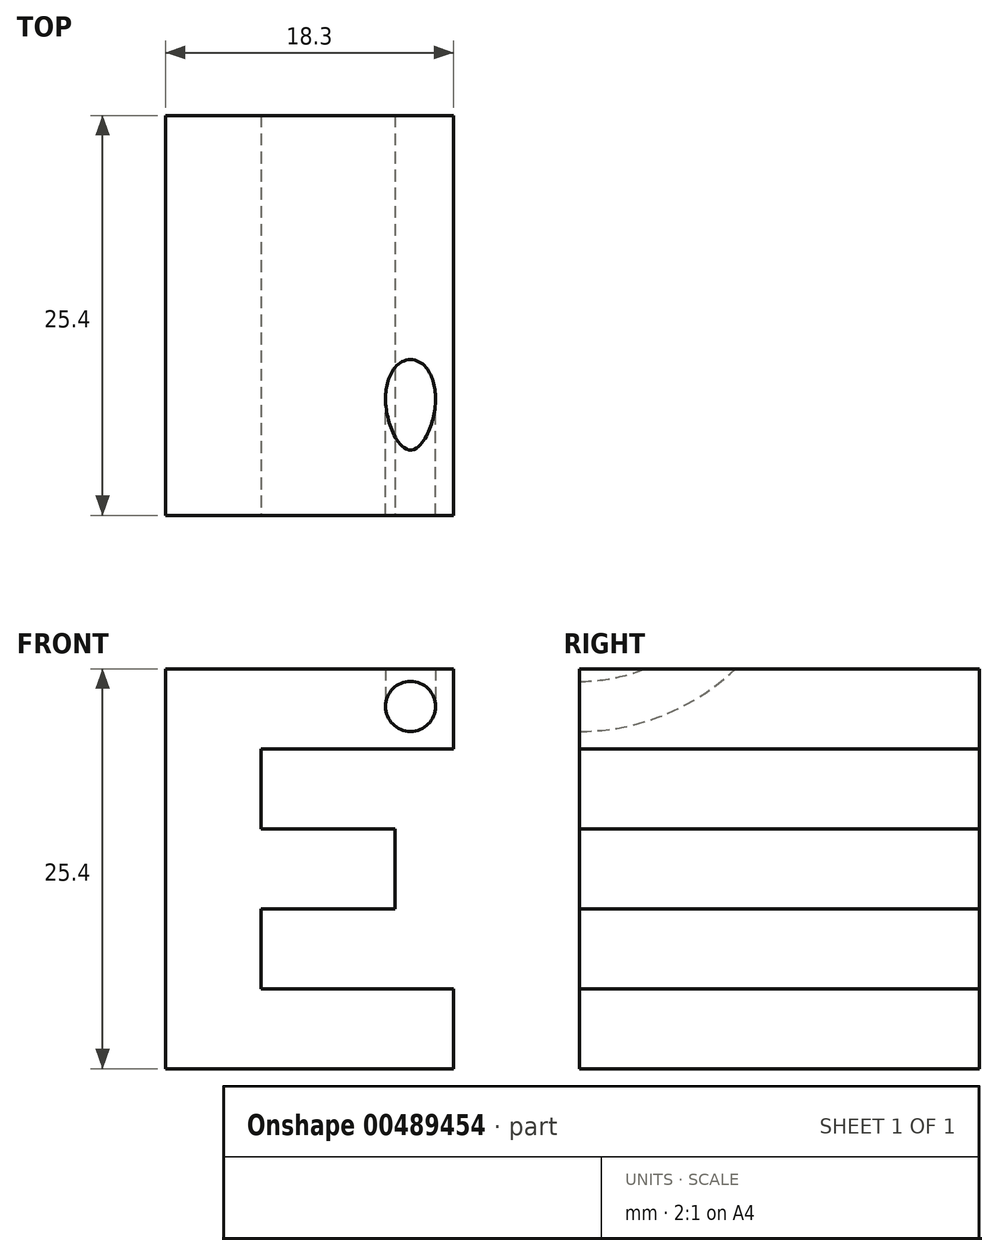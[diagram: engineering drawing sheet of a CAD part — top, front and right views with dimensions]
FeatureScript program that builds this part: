
annotation { "Feature Type Name" : "Feature", "Feature Type Description" : "" }
export const myFeature = defineFeature(function(context is Context, id is Id, definition is map)
    precondition{}
    {
        {
            var Q0;
            Q0=qCreatedBy(makeId("Front.planeOp"),FACE);
            var sketch = newSketch(context, id + "F0", { "sketchPlane" : qUnion([Q0])});
            skLineSegment(sketch, "E0", {"start": v(0, 0) * mm, "end": v(25.4, 0) * mm});
            skLineSegment(sketch, "E1", {"start": v(25.4, 0) * mm, "end": v(25.4, 25.4) * mm});
            skLineSegment(sketch, "E2", {"start": v(25.4, 25.4) * mm, "end": v(0, 25.4) * mm});
            skLineSegment(sketch, "E3", {"start": v(0, 25.4) * mm, "end": v(0, 0) * mm});
            skSolve(sketch);
        }
        {
            var Q0;
            Q0=makeQuery(id+"F0.imprint","IMPRINT",FACE,{"disambiguationData":[TD([[makeQuery(id+"F0.imprint","IMPRINT",EDGE,{"derivedFrom":sQuery(id+"F0.wireOp",EDGE,"E0")}),1.0]])]});
            extrude(context, id + "F1", {"entities" : qUnion([Q0]), "depth" : 25.4 * mm, "offsetDistance" : 25.4 * mm});
        }
        {
            var Q0;
            Q0=makeQuery(id+"F1.opExtrude","CAP_FACE",FACE,{"disambiguationData":[OSD([sQuery(id+"F0.wireOp",EDGE,"E0"),sQuery(id+"F0.wireOp",EDGE,"E1"),sQuery(id+"F0.wireOp",EDGE,"E2"),sQuery(id+"F0.wireOp",EDGE,"E3")])],"isStart":false});
            var sketch = newSketch(context, id + "F2", { "sketchPlane" : qUnion([Q0])});
            skLineSegment(sketch, "E4", {"start": v(4.03, 25.4) * mm, "end": v(4.03, 0) * mm});
            skLineSegment(sketch, "E5", {"start": v(4.03, 0) * mm, "end": v(22.33, 0) * mm});
            skLineSegment(sketch, "E6", {"start": v(10.1, 10.16) * mm, "end": v(18.62, 10.16) * mm});
            skLineSegment(sketch, "E7", {"start": v(18.62, 10.16) * mm, "end": v(18.62, 15.24) * mm});
            skLineSegment(sketch, "E8", {"start": v(18.62, 15.24) * mm, "end": v(10.1, 15.24) * mm});
            skLineSegment(sketch, "E9", {"start": v(10.1, 15.24) * mm, "end": v(10.1, 20.32) * mm});
            skLineSegment(sketch, "E10", {"start": v(10.1, 20.32) * mm, "end": v(22.33, 20.32) * mm});
            skLineSegment(sketch, "E11", {"start": v(22.33, 20.32) * mm, "end": v(22.33, 25.4) * mm});
            skLineSegment(sketch, "E12", {"start": v(22.33, 0) * mm, "end": v(22.33, 5.08) * mm});
            skLineSegment(sketch, "E13", {"start": v(22.33, 5.08) * mm, "end": v(10.1, 5.08) * mm});
            skLineSegment(sketch, "E14", {"start": v(10.1, 5.08) * mm, "end": v(10.1, 10.16) * mm});
            skLineSegment(sketch, "E15", {"start": v(22.33, 25.4) * mm, "end": v(4.03, 25.4) * mm});
            skSolve(sketch);
        }
        {
            var Q0;
            {var subQ0=sQuery(id+"F2.wireOp",EDGE,"E4");Q0=makeQuery(id+"F2.imprint","IMPRINT",FACE,{"disambiguationData":[TD([[makeQuery(id+"F2.imprint","IMPRINT",EDGE,{"derivedFrom":subQ0}),-1.0]])]});}
            var Q1;
            Q1=makeQuery(id+"F2.imprint","IMPRINT",FACE,{"disambiguationData":[TD([[makeQuery(id+"F2.imprint","IMPRINT",EDGE,{"derivedFrom":sQuery(id+"F2.wireOp",EDGE,"E6")}),-1.0]])]});
            extrude(context, id + "F3", {"entities" : qUnion([Q0, Q1]), "operationType" : NewBodyOperationType.REMOVE, "oppositeDirection" : true, "depth" : 25.4 * mm, "offsetDistance" : 25.4 * mm});
        }
        {
            var Q0;
            Q0=makeQuery(id+"F1.opExtrude","CAP_FACE",FACE,{"disambiguationData":[OSD([sQuery(id+"F0.wireOp",EDGE,"E0"),sQuery(id+"F0.wireOp",EDGE,"E1"),sQuery(id+"F0.wireOp",EDGE,"E2"),sQuery(id+"F0.wireOp",EDGE,"E3")])],"isStart":false});
            var sketch = newSketch(context, id + "F4", { "sketchPlane" : qUnion([Q0])});
            skCircle(sketch, "E16", {"center": v(19.6, 23.01) * mm, "radius": 1.59 * mm});
            skLineSegment(sketch, "E17", {"start": v(14.1, 35.71) * mm, "end": v(25.53, 35.71) * mm});
            skSolve(sketch);
        }
        {
            var Q0;
            Q0 = qSketchRegion(id + "F4", true);
            var Q1;
            Q1=sQuery(id+"F4.wireOp",EDGE,"E17");
            revolve(context, id + "F5", {"operationType" : NewBodyOperationType.REMOVE, "entities" : qUnion([Q0]), "axis" : qUnion([Q1]), "revolveType" : RevolveType.FULL, "oppositeDirection" : true});
        }
    });
